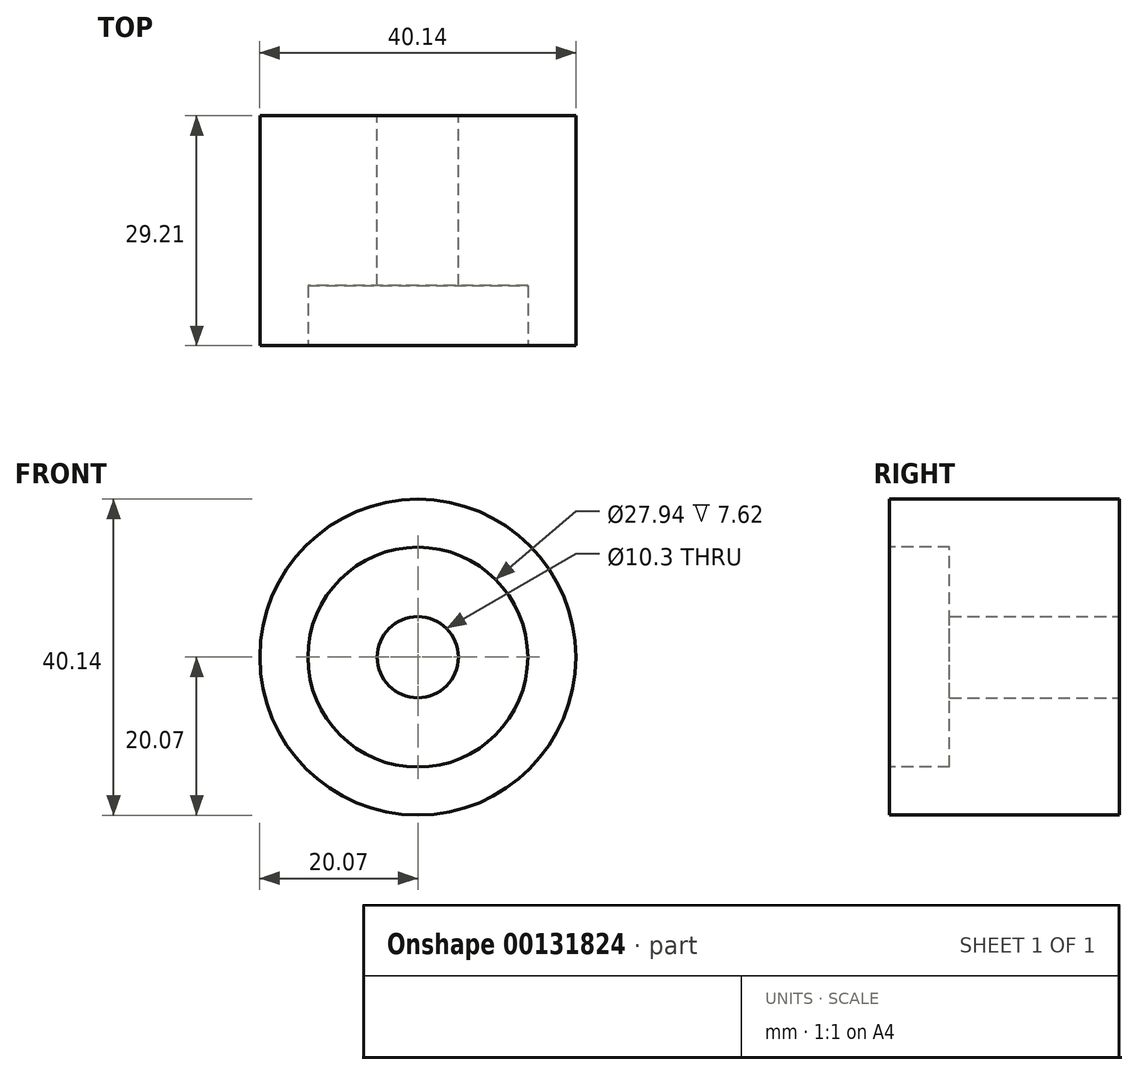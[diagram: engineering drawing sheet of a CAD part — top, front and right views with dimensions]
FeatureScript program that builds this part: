
annotation { "Feature Type Name" : "Feature", "Feature Type Description" : "" }
export const myFeature = defineFeature(function(context is Context, id is Id, definition is map)
    precondition{}
    {
        {
            var Q0;
            Q0=qCreatedBy(makeId("Front.planeOp"),FACE);
            var sketch = newSketch(context, id + "F0", { "sketchPlane" : qUnion([Q0])});
            skCircle(sketch, "E0", {"center": v(0, 0) * mm, "radius": 20.07 * mm});
            skSolve(sketch);
        }
        {
            var Q0;
            Q0=makeQuery(id+"F0.imprint","IMPRINT",FACE,{"disambiguationData":[TD([[makeQuery(id+"F0.imprint","IMPRINT",EDGE,{"derivedFrom":sQuery(id+"F0.wireOp",EDGE,"E0")}),1.0]])]});
            extrude(context, id + "F1", {"entities" : qUnion([Q0]), "depth" : 29.2 * mm});
        }
        {
            var Q0;
            Q0=makeQuery(id+"F1.opExtrude","CAP_FACE",FACE,{"disambiguationData":[OSD([sQuery(id+"F0.wireOp",EDGE,"E0")])],"isStart":false});
            var sketch = newSketch(context, id + "F2", { "sketchPlane" : qUnion([Q0])});
            skCircle(sketch, "E1", {"center": v(0, 0) * mm, "radius": 13.97 * mm});
            skSolve(sketch);
        }
        {
            var Q0;
            Q0=makeQuery(id+"F2.imprint","IMPRINT",FACE,{"disambiguationData":[TD([[makeQuery(id+"F2.imprint","IMPRINT",EDGE,{"derivedFrom":sQuery(id+"F2.wireOp",EDGE,"E1")}),1.0]])]});
            extrude(context, id + "F3", {"entities" : qUnion([Q0]), "operationType" : NewBodyOperationType.REMOVE, "oppositeDirection" : true, "depth" : 7.62 * mm});
        }
        {
            var Q0;
            Q0=makeQuery(id+"F1.opExtrude","CAP_FACE",FACE,{"disambiguationData":[OSD([sQuery(id+"F0.wireOp",EDGE,"E0")])],"isStart":true});
            var sketch = newSketch(context, id + "F4", { "sketchPlane" : qUnion([Q0])});
            skPoint(sketch, "E2", {"position": v(0, 0) * mm});
            skSolve(sketch);
        }
        {
            var Q0;
            Q0=sQuery(id+"F4.wireOp",VERTEX,"E2");
            var Q1;
            Q1=makeQuery(id+"F1.opExtrude","SWEPT_BODY",BODY,{"disambiguationData":[OSD([sQuery(id+"F0.wireOp",EDGE,"E0")])]});
            hole(context, id + "F5", {"style" : HoleStyle.SIMPLE, "endStyle" : HoleEndStyle.THROUGH, "standardTappedOrClearance" : lookupTablePath({ "standard" : "ISO", "engagement" : "75%", "pitch" : "1.75 mm", "size" : "M12", "type" : "Tapped" }), "standardBlindInLast" : lookupTablePath({ "standard" : "ISO", "engagement" : "75%", "pitch" : "1.75 mm", "size" : "M12", "type" : "Tapped" }), "holeDiameter" : 10.3 * mm, "locations" : qUnion([Q0]), "scope" : qUnion([Q1]), "isTappedThrough" : true, "majorDiameter" : 12 * mm, "showTappedDepth" : true});
        }
    });
